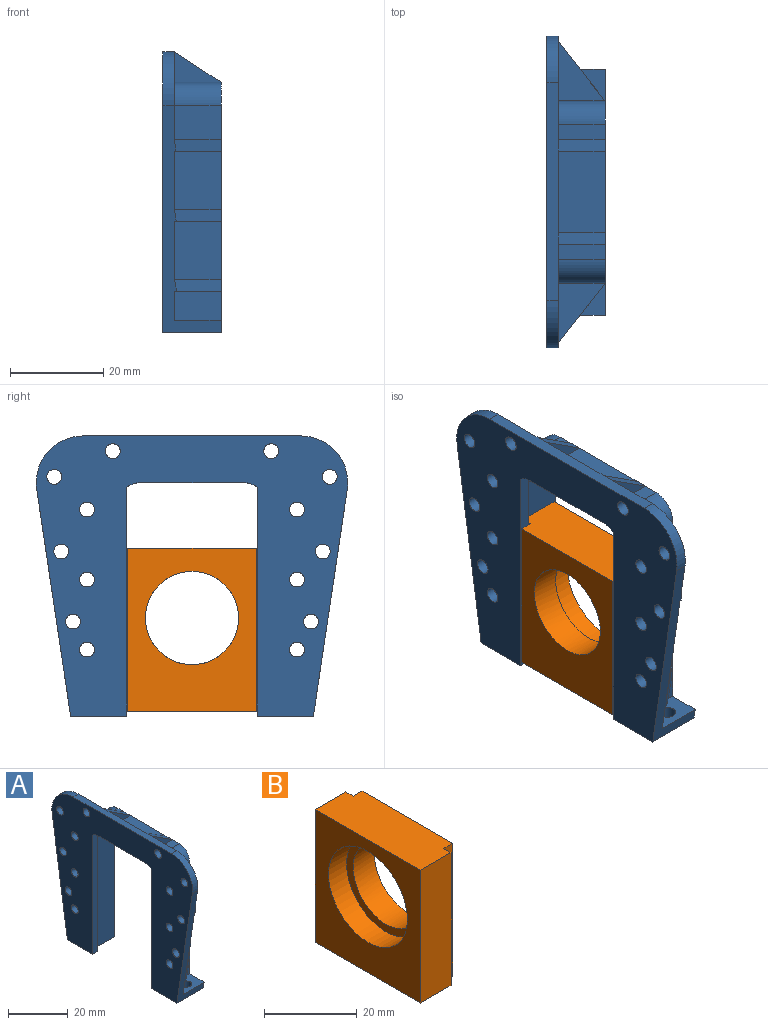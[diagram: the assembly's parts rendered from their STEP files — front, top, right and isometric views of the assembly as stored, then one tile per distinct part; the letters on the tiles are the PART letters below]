
ASSEMBLY  parts=2 mates=1
PART A: 82 faces, bbox 12.5x66.7x60 mm
  f0: plane 45x10mm, normal (0,-1,0), area 450mm2, adj f3,f4,f49,f80
  f1: plane 66.74x60mm, normal (-1,0,0), area 2087.6mm2, adj f2,f3,f42,f43,f44,f45,f46,f47
  f2: plane 12.5x12mm, normal (0,0,-1), area 119.8mm2, adj f1,f4,f41,f47,f76,f78,f79
  f3: plane 12.5x12mm, normal (0,0,-1), area 119.8mm2, adj f0,f1,f4,f43,f77,f80,f81
  f4: plane 53.5x52.75mm, normal (1,0,0), area 519.9mm2, adj f0,f2,f3,f5,f6,f7,f8,f9
  f5: plane 12.67x10mm, normal (0.78,-0.62,0), area 39.8mm2, adj f4,f21,f22,f47
  f6: plane 10x8.18mm, normal (0.63,-0.77,0), area 31.6mm2, adj f4,f19,f20,f47
  f7: plane 10.43x10mm, normal (0.72,-0.69,0), area 35.5mm2, adj f4,f13,f14,f47
  f8: plane 10x6.87mm, normal (0,0,1), area 58.6mm2, adj f4,f11,f12,f43,f77
  f9: plane 10x6.87mm, normal (0,0,1), area 58.6mm2, adj f4,f10,f32,f47,f76
  f10: plane 10x6.25mm, normal (0,-1,0), area 62.5mm2, adj f4,f9,f20,f32
  f11: plane 10x6.25mm, normal (0,1,0), area 62.5mm2, adj f4,f8,f12,f17
  f12: plane 7.81x6.25mm, normal (1,0,0), area 45.9mm2, adj f8,f11,f17,f43
  f13: plane 10.43x10mm, normal (0,0,1), area 52.1mm2, adj f7,f33,f36
  f14: plane 10.05x10mm, normal (0,0,-1), area 52.1mm2, adj f7,f31,f34,f47
  f15: plane 10x8.18mm, normal (0,0,1), area 40.9mm2, adj f25,f26,f61
  f16: plane 10.43x10mm, normal (0,0,1), area 52.1mm2, adj f27,f28,f60
  f17: plane 10x7.81mm, normal (0,0,-1), area 40.8mm2, adj f11,f12,f43,f61
  f18: plane 12.67x10mm, normal (0,0,1), area 63.4mm2, adj f29,f30,f59
  f19: plane 10x8.18mm, normal (0,0,1), area 40.9mm2, adj f6,f31,f34
  f20: plane 10x7.81mm, normal (0,0,-1), area 40.8mm2, adj f6,f10,f32,f47
  f21: plane 12.67x10mm, normal (0,0,1), area 63.4mm2, adj f5,f35,f40
  f22: plane 12.3x10mm, normal (0,0,-1), area 63.3mm2, adj f5,f33,f36,f47
  f23: plane 10x6.5mm, normal (0,1,0), area 32.5mm2, adj f30,f51,f58
  f24: plane 10x6.5mm, normal (0,1,0), area 32.5mm2, adj f37,f38,f57
  f25: plane 12.5x10mm, normal (0,1,0), area 125mm2, adj f4,f15,f26,f56
  f26: plane 12.5x10.05mm, normal (1,0,0), area 97.9mm2, adj f15,f25,f43,f56,f68,f69
  f27: plane 12.5x10mm, normal (0,1,0), area 125mm2, adj f4,f16,f28,f55
  f28: plane 12.5x12.3mm, normal (1,0,0), area 125.9mm2, adj f16,f27,f43,f55,f63,f70
  f29: plane 10x7.25mm, normal (0,1,0), area 72.5mm2, adj f4,f18,f30,f50
  f30: plane 22.12x18.75mm, normal (1,0,0), area 268.6mm2, adj f18,f23,f29,f43,f44,f45,f50,f51
  f31: plane 12.5x10mm, normal (0,-1,0), area 125mm2, adj f4,f14,f19,f34
  f32: plane 7.81x6.25mm, normal (1,0,0), area 45.9mm2, adj f9,f10,f20,f47
  f33: plane 12.5x10mm, normal (0,-1,0), area 125mm2, adj f4,f13,f22,f36
  f34: plane 12.5x10.05mm, normal (1,0,0), area 97.9mm2, adj f14,f19,f31,f47,f66,f74
  f35: plane 10x7.25mm, normal (0,-1,0), area 72.5mm2, adj f4,f21,f40,f52
  f36: plane 12.5x12.3mm, normal (1,0,0), area 125.9mm2, adj f13,f22,f33,f47,f65,f73
  f37: plane 17.5x10mm, normal (0,0,1), area 175mm2, adj f4,f24,f38,f54
  f38: plane 17.5x6.5mm, normal (1,0,0), area 113.7mm2, adj f24,f37,f45,f54
  f39: plane 10x3.25mm, normal (0,0,1), area 32.5mm2, adj f4,f40,f52,f53
  f40: plane 22.12x18.75mm, normal (1,0,0), area 268.6mm2, adj f21,f35,f39,f45,f46,f47,f52,f53
  f41: plane 45x10mm, normal (0,1,0), area 450mm2, adj f2,f4,f48,f78
  f42: plane 22x12.5mm, normal (0,0,-1), area 275mm2, adj f1,f4,f48,f49
  f43: plane 48.52x12.5mm, normal (0,0.99,-0.15), area 149.3mm2, adj f1,f3,f4,f8,f12,f17,f26,f28
  f44: cylinder r=10mm len=11.48mm, axis (-1,0,0), area 43mm2, adj f1,f30,f43,f45
  f45: plane 46.74x2.5mm, normal (0,0,1), area 116.8mm2, adj f1,f30,f38,f40,f44,f46,f57,f58
  f46: cylinder r=10mm len=11.48mm, axis (-1,0,0), area 43mm2, adj f1,f40,f45,f47
  f47: plane 48.52x12.5mm, normal (0,-0.99,-0.15), area 149.3mm2, adj f1,f2,f4,f5,f6,f7,f9,f14
  f48: cylinder r=5mm len=12.5mm, axis (-1,0,0), area 86.6mm2, adj f1,f4,f41,f42,f78,f79
  f49: cylinder r=5mm len=12.5mm, axis (1,0,0), area 86.6mm2, adj f0,f1,f4,f42,f80,f81
  f50: cylinder r=5mm len=10mm, axis (-1,0,0), area 78.5mm2, adj f4,f29,f30,f51
  f51: plane 10x3.25mm, normal (0,0,1), area 32.5mm2, adj f4,f23,f30,f50
  f52: cylinder r=5mm len=10mm, axis (-1,0,0), area 78.5mm2, adj f4,f35,f39,f40
  f53: plane 10x6.5mm, normal (0,-1,0), area 32.5mm2, adj f39,f40,f57
  f54: plane 10x6.5mm, normal (0,-1,0), area 32.5mm2, adj f37,f38,f58
  f55: plane 12.3x10mm, normal (0,0,-1), area 63.3mm2, adj f27,f28,f43,f59
  f56: plane 10.05x10mm, normal (0,0,-1), area 52.1mm2, adj f25,f26,f43,f60
  f57: plane 10x6.5mm, normal (0.54,0,0.84), area 29.8mm2, adj f4,f24,f45,f53
  f58: plane 10x6.5mm, normal (0.54,0,0.84), area 29.8mm2, adj f4,f23,f45,f54
  f59: plane 12.67x10mm, normal (0.78,0.62,0), area 39.8mm2, adj f4,f18,f43,f55
  f60: plane 10.43x10mm, normal (0.72,0.69,0), area 35.5mm2, adj f4,f16,f43,f56
  f61: plane 10x8.18mm, normal (0.63,0.77,0), area 31.6mm2, adj f4,f15,f17,f43
  f62: cylinder r=1.6mm len=3.2mm, axis (1,0,0), area 25.1mm2, adj f1,f40
  f63: cylinder r=1.6mm len=3.2mm, axis (1,0,0), area 25.1mm2, adj f1,f28
  f64: cylinder r=1.6mm len=3.2mm, axis (1,0,0), area 25.1mm2, adj f1,f30
  f65: cylinder r=1.6mm len=3.2mm, axis (1,0,0), area 25.1mm2, adj f1,f36
  f66: cylinder r=1.6mm len=3.2mm, axis (1,0,0), area 25.1mm2, adj f1,f34
  f67: cylinder r=1.6mm len=3.2mm, axis (1,0,0), area 25.1mm2, adj f1,f40
  f68: cylinder r=1.6mm len=3.2mm, axis (1,0,0), area 25.1mm2, adj f1,f26
  f69: cylinder r=1.6mm len=3.2mm, axis (1,0,0), area 25.1mm2, adj f1,f26
  f70: cylinder r=1.6mm len=3.2mm, axis (1,0,0), area 25.1mm2, adj f1,f28
  f71: cylinder r=1.6mm len=3.2mm, axis (1,0,0), area 25.1mm2, adj f1,f30
  f72: cylinder r=1.6mm len=3.2mm, axis (1,0,0), area 25.1mm2, adj f1,f40
  f73: cylinder r=1.6mm len=3.2mm, axis (1,0,0), area 25.1mm2, adj f1,f36
  f74: cylinder r=1.6mm len=3.2mm, axis (1,0,0), area 25.1mm2, adj f1,f34
  f75: cylinder r=1.6mm len=3.2mm, axis (1,0,0), area 25.1mm2, adj f1,f30
  f76: cylinder r=1.8mm len=3.6mm, axis (0,0,1), area 28.3mm2, adj f2,f9
  f77: cylinder r=1.8mm len=3.6mm, axis (0,0,1), area 28.3mm2, adj f3,f8
  f78: plane 49x2mm, normal (1,0,0), area 95.6mm2, adj f2,f41,f48,f79
  f79: plane 49x2.5mm, normal (0,1,0), area 122.5mm2, adj f1,f2,f48,f78
  f80: plane 49x2mm, normal (1,0,0), area 95.6mm2, adj f0,f3,f49,f81
  f81: plane 49x2.5mm, normal (0,-1,0), area 122.5mm2, adj f1,f3,f49,f80
PART B: 13 faces, bbox 12x32x35 mm
  f0: cylinder r=10mm len=20mm, axis (-1,0,0), area 408.4mm2, adj f2,f12
  f1: plane 32x12mm, normal (0,0,1), area 372.1mm2, adj f2,f4,f5,f6,f7,f8,f9,f10
  f2: plane 35x27.6mm, normal (1,0,0), area 651.8mm2, adj f0,f1,f3,f7,f9
  f3: plane 32x12mm, normal (0,0,-1), area 372.1mm2, adj f2,f4,f5,f6,f7,f8,f9,f10
  f4: plane 35x9.3mm, normal (0,-1,0), area 325.5mm2, adj f1,f3,f6,f10
  f5: plane 35x9.3mm, normal (0,1,0), area 325.5mm2, adj f1,f3,f6,f8
  f6: plane 35x32mm, normal (-1,0,0), area 667.6mm2, adj f1,f3,f4,f5,f11
  f7: plane 35x2.7mm, normal (0,1,0), area 94.5mm2, adj f1,f2,f3,f8
  f8: plane 35x2.2mm, normal (1,0,0), area 77mm2, adj f1,f3,f5,f7
  f9: plane 35x2.7mm, normal (0,-1,0), area 94.5mm2, adj f1,f2,f3,f10
  f10: plane 35x2.2mm, normal (1,0,0), area 77mm2, adj f1,f3,f4,f9
  f11: cylinder r=12mm len=24mm, axis (-1,0,0), area 414.7mm2, adj f6,f12
  f12: plane 24x24mm, normal (-1,0,0), area 138.2mm2, adj f0,f11
PLACE A t=(-25.56,-21.03,9.42)mm
PLACE B rot(axis=(0,0,1),180deg) t=(-13.45,-1.71,0.28)mm
MATE slider B.f1 <-> A.f42  axis (0,0,1) through (-19.31,-8.34,-6.95)mm
